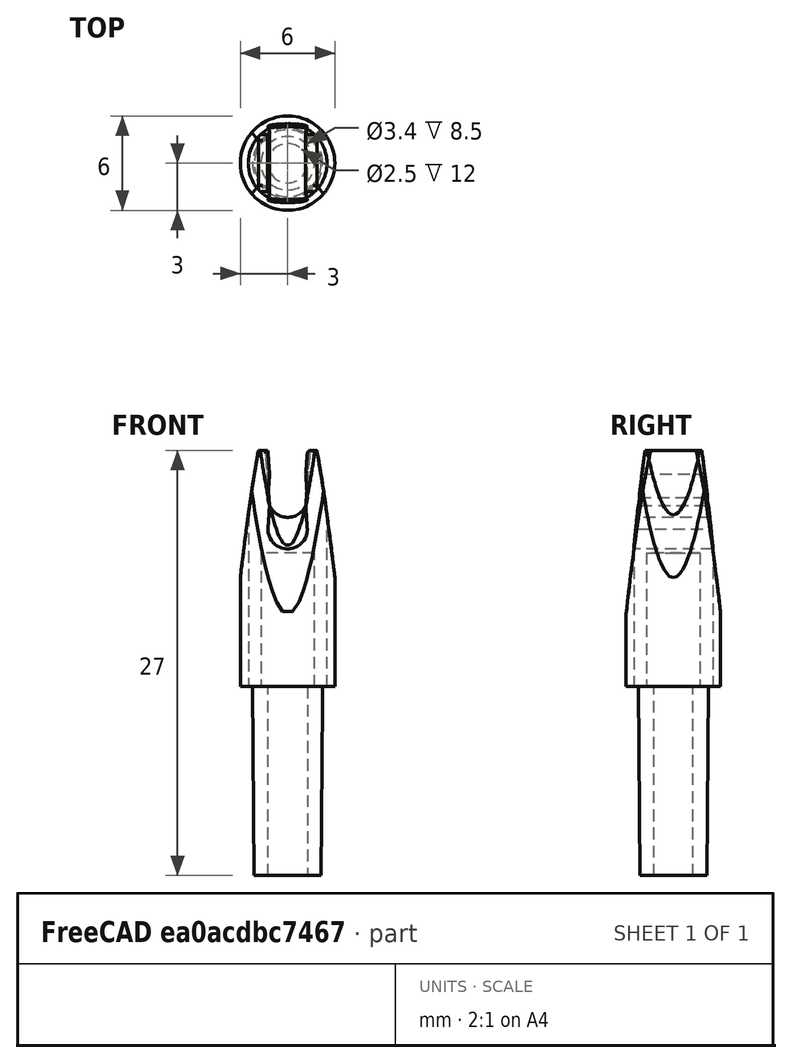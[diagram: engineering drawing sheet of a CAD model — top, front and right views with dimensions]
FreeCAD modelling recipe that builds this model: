
FCSTD DOCUMENT  (FreeCAD 0.20R26155 (Git))
Label: 4mm Pole Nock and 3mm Pin Nock
License: Creative Commons Attribution
LicenseURL: http://creativecommons.org/licenses/by/4.0/
objects: Sketcher::SketchObject×12, PartDesign::Pocket×8, PartDesign::Pad×3, PartDesign::Fillet×2, PartDesign::Body×2, Mesh::Feature×2
note: 40 computed .brp shape members not serialized (recipe doc carries the construction recipe); baked Part::Feature solids carry a one-line shape summary decoded from their .brp

FEATURE [Sketcher::SketchObject] Sketch
  FullyConstrained = true
  MapMode = 5
  Support = -> [XY_Plane]
  sketch-geometry (1):
    g0: Circle CenterX=0 CenterY=0 CenterZ=0 NormalX=0 NormalY=0 NormalZ=1 AngleXU=0 Radius=3
  constraints (2):
    c: Coincident(g0,g-1)
    c: Diameter(g0) = 6
FEATURE [PartDesign::Pad] Pad
  Direction = (0,0,1)
  Length = 15
  Length2 = 100
  Profile = -> Sketch
  Type = 0
FEATURE [Sketcher::SketchObject] Sketch001
  FullyConstrained = true
  MapMode = 5
  Placement = pos=(0,0,0) rot=(1,0,0;1.5708rad)
  Support = -> [XZ_Plane]
  sketch-geometry (6):
    g0: ArcOfCircle CenterX=0 CenterY=10 CenterZ=0 NormalX=0 NormalY=0 NormalZ=1 AngleXU=0 Radius=1.25 StartAngle=3.14159 EndAngle=6.28319
    g1: LineSegment StartX=-1.15 StartY=11.5 StartZ=0 EndX=-1.75 EndY=19.5 EndZ=0
    g2: LineSegment StartX=-1.75 StartY=19.5 StartZ=0 EndX=1.75 EndY=19.5 EndZ=0
    g3: LineSegment StartX=1.75 StartY=19.5 StartZ=0 EndX=1.15 EndY=11.5 EndZ=0
    g4: LineSegment StartX=1.15 StartY=11.5 StartZ=0 EndX=1.25 EndY=10 EndZ=0
    g5: LineSegment StartX=-1.15 StartY=11.5 StartZ=0 EndX=-1.25 EndY=10 EndZ=0
  constraints (17):
    c: PointOnObject(g0,g-2)
    c: Horizontal(g0,g0)
    c: Horizontal(g0,g0)
    c: DistanceX(g0,g0) = 2.5
    c: Coincident(g1,g2)
    c: Coincident(g2,g3)
    c: Coincident(g3,g4)
    c: Coincident(g4,g0)
    c: Coincident(g5,g1)
    c: Coincident(g5,g0)
    c: Symmetric(g1,g3,g-2)
    c: Symmetric(g2,g1,g-2)
    c: DistanceY(g-1,g0) = 10
    c: DistanceY(g0,g3) = 1.5
    c: DistanceY(g3,g2) = 8
    c: DistanceX(g2,g2) = 3.5
    c: DistanceX(g1,g3) = 2.3
FEATURE [PartDesign::Pocket] Pocket
  BaseFeature = -> Pad
  Length = 7
  Length2 = 100
  Midplane = true
  Profile = -> Sketch001
  Type = 0
FEATURE [Sketcher::SketchObject] Sketch002
  FullyConstrained = true
  MapMode = 5
  Support = -> [XY_Plane]
  sketch-geometry (1):
    g0: Circle CenterX=0 CenterY=0 CenterZ=0 NormalX=0 NormalY=0 NormalZ=1 AngleXU=0 Radius=2.225
  constraints (2):
    c: Coincident(g0,g-1)
    c: Diameter(g0) = 4.45
FEATURE [PartDesign::Pad] Pad001
  BaseFeature = -> Pocket
  Direction = (0,0,1)
  Length = 12
  Length2 = 100
  Profile = -> Sketch002
  ReferenceAxis = -> Sketch002 [N_Axis]
  Reversed = true
  Type = 0
FEATURE [Sketcher::SketchObject] Sketch003
  FullyConstrained = true
  MapMode = 5
  Support = -> [XY_Plane]
  sketch-geometry (1):
    g0: Circle CenterX=0 CenterY=0 CenterZ=0 NormalX=0 NormalY=0 NormalZ=1 AngleXU=0 Radius=1.25
  constraints (2):
    c: Coincident(g0,g-1)
    c: Diameter(g0) = 2.5
FEATURE [PartDesign::Pocket] Pocket001
  BaseFeature = -> Pad001
  Length = 18
  Length2 = 100
  Profile = -> Sketch003
  Type = 0
FEATURE [PartDesign::Fillet] Fillet  label="fillet"
  Base = -> Pocket001 [Face9,Edge17,Face3]
  BaseFeature = -> Pocket001
  Radius = 0.2
  SupportTransform = false
FEATURE [Sketcher::SketchObject] Sketch004
  FullyConstrained = false
  MapMode = 5
  Placement = pos=(0,0,0) rot=(1,0,0;1.5708rad)
  Support = -> [XZ_Plane]
  sketch-geometry (11):
    g0: LineSegment StartX=-6 StartY=4 StartZ=0 EndX=-6 EndY=22 EndZ=0
    g1: LineSegment StartX=-6 StartY=22 StartZ=0 EndX=6 EndY=22 EndZ=0
    g2: LineSegment StartX=6 StartY=22 StartZ=0 EndX=6 EndY=4 EndZ=0
    g3: LineSegment StartX=-6 StartY=4 StartZ=0 EndX=-3.31793 EndY=4 EndZ=0
    g4: LineSegment StartX=6 StartY=4 StartZ=0 EndX=3.31793 EndY=4 EndZ=0
    g5: Circle CenterX=-3.31793 CenterY=4 CenterZ=0 NormalX=0 NormalY=0 NormalZ=1 AngleXU=0 Radius=1
    g6: Circle CenterX=0 CenterY=36 CenterZ=0 NormalX=0 NormalY=0 NormalZ=1 AngleXU=0 Radius=1
    g7: Circle CenterX=3.31793 CenterY=4 CenterZ=0 NormalX=0 NormalY=0 NormalZ=1 AngleXU=0 Radius=1
    g8: BSplineCurve PolesCount=3 KnotsCount=2 Degree=2 IsPeriodic=0
    g9: GeomPoint X=-3.31793 Y=4 Z=0
    g10: GeomPoint X=3.31793 Y=4 Z=0
  constraints (24):
    c: Vertical(g0)
    c: Coincident(g0,g1)
    c: Coincident(g1,g2)
    c: Symmetric(g2,g0,g-2)
    c: Symmetric(g0,g1,g-2)
    c: Coincident(g3,g0)
    c: Horizontal(g3)
    c: Coincident(g4,g2)
    c: Symmetric(g3,g4,g-2)
    c: Coincident(g8,g3)
    c: Weight(g5) = 1
    c: Equal(g5,g6)
    c: PointOnObject(g6,g-2)
    c: Equal(g5,g7)
    c: Coincident(g8,g4)
    c: InternalAlignment(g5,g8)
    c: InternalAlignment(g6,g8)
    c: InternalAlignment(g7,g8)
    c: InternalAlignment(g9,g8)
    c: InternalAlignment(g10,g8)
    c: DistanceY(g-1,g0) = 4
    c: DistanceX(g1,g1) = 12
    c: DistanceY(g-1,g6) = 36
    c: DistanceY(g0,g0) = 18
FEATURE [PartDesign::Pocket] Pocket002
  BaseFeature = -> Fillet
  Length = 10
  Length2 = 100
  Midplane = true
  Profile = -> Sketch004
  Type = 0
FEATURE [Sketcher::SketchObject] Sketch005
  FullyConstrained = false
  MapMode = 5
  Placement = pos=(0,0,0) rot=(0.57735,0.57735,0.57735;2.0944rad)
  Support = -> [YZ_Plane]
  sketch-geometry (11):
    g0: LineSegment StartX=-3.13174 StartY=3.4287 StartZ=0 EndX=-10.6002 EndY=3.4287 EndZ=0
    g1: LineSegment StartX=-10.6002 StartY=3.4287 StartZ=0 EndX=-10.6002 EndY=40.5505 EndZ=0
    g2: LineSegment StartX=-10.6002 StartY=40.5505 StartZ=0 EndX=10.6002 EndY=40.5505 EndZ=0
    g3: LineSegment StartX=10.6002 StartY=40.5505 StartZ=0 EndX=10.6002 EndY=3.4287 EndZ=0
    g4: LineSegment StartX=10.6002 StartY=3.4287 StartZ=0 EndX=3.13174 EndY=3.4287 EndZ=0
    g5: Circle CenterX=-3.13174 CenterY=3.4287 CenterZ=0 NormalX=0 NormalY=0 NormalZ=1 AngleXU=0 Radius=1
    g6: Circle CenterX=0 CenterY=32.7419 CenterZ=0 NormalX=0 NormalY=0 NormalZ=1 AngleXU=0 Radius=1
    g7: Circle CenterX=3.13174 CenterY=3.4287 CenterZ=0 NormalX=0 NormalY=0 NormalZ=1 AngleXU=0 Radius=1
    g8: BSplineCurve PolesCount=3 KnotsCount=2 Degree=2 IsPeriodic=0
    g9: GeomPoint X=-3.13174 Y=3.4287 Z=0
    g10: GeomPoint X=3.13174 Y=3.4287 Z=0
  constraints (21):
    c: Horizontal(g0)
    c: Coincident(g0,g1)
    c: Vertical(g1)
    c: Coincident(g1,g2)
    c: Coincident(g2,g3)
    c: Vertical(g3)
    c: Coincident(g3,g4)
    c: Horizontal(g4)
    c: Symmetric(g0,g4,g-2)
    c: Symmetric(g1,g2,g-2)
    c: Coincident(g8,g0)
    c: Weight(g5) = 1
    c: Equal(g5,g6)
    c: PointOnObject(g6,g-2)
    c: Equal(g5,g7)
    c: Coincident(g8,g4)
    c: InternalAlignment(g5,g8)
    c: InternalAlignment(g6,g8)
    c: InternalAlignment(g7,g8)
    c: InternalAlignment(g9,g8)
    c: InternalAlignment(g10,g8)
FEATURE [PartDesign::Pocket] Pocket003  label="4mm Poll Nock"
  BaseFeature = -> Pocket002
  Length = 9
  Length2 = 100
  Midplane = true
  Profile = -> Sketch005
  Type = 0
FEATURE [PartDesign::Body] Body
  Group = -> [Sketch,Pad,Sketch001,Pocket,Sketch002,Pad001,Sketch003,Pocket001,Fillet,Sketch004,Pocket002,Sketch005,Pocket003]
  Origin = -> Origin
  Tip = -> Pocket003
FEATURE [Sketcher::SketchObject] Sketch006
  FullyConstrained = true
  MapMode = 5
  Support = -> [XY_Plane001]
  sketch-geometry (1):
    g0: Circle CenterX=0 CenterY=0 CenterZ=0 NormalX=0 NormalY=0 NormalZ=1 AngleXU=0 Radius=1.7
  constraints (2):
    c: Coincident(g0,g-1)
    c: Diameter(g0) = 3.4
FEATURE [Sketcher::SketchObject] Sketch007
  FullyConstrained = true
  MapMode = 5
  Placement = pos=(0,0,0) rot=(1,0,0;1.5708rad)
  Support = -> [XZ_Plane001]
  sketch-geometry (6):
    g0: ArcOfCircle CenterX=0 CenterY=12 CenterZ=0 NormalX=0 NormalY=0 NormalZ=1 AngleXU=0 Radius=1.25 StartAngle=3.14159 EndAngle=6.28319
    g1: LineSegment StartX=-1.15 StartY=13.5 StartZ=0 EndX=-1.75 EndY=21.5 EndZ=0
    g2: LineSegment StartX=-1.75 StartY=21.5 StartZ=0 EndX=1.75 EndY=21.5 EndZ=0
    g3: LineSegment StartX=1.75 StartY=21.5 StartZ=0 EndX=1.15 EndY=13.5 EndZ=0
    g4: LineSegment StartX=1.15 StartY=13.5 StartZ=0 EndX=1.25 EndY=12 EndZ=0
    g5: LineSegment StartX=-1.15 StartY=13.5 StartZ=0 EndX=-1.25 EndY=12 EndZ=0
  constraints (17):
    c: PointOnObject(g0,g-2)
    c: Horizontal(g0,g0)
    c: Horizontal(g0,g0)
    c: DistanceX(g0,g0) = 2.5
    c: Coincident(g1,g2)
    c: Coincident(g2,g3)
    c: Coincident(g3,g4)
    c: Coincident(g4,g0)
    c: Coincident(g5,g1)
    c: Coincident(g5,g0)
    c: Symmetric(g1,g3,g-2)
    c: Symmetric(g2,g1,g-2)
    c: DistanceY(g-1,g0) = 12
    c: DistanceY(g0,g3) = 1.5
    c: DistanceY(g3,g2) = 8
    c: DistanceX(g2,g2) = 3.5
    c: DistanceX(g1,g3) = 2.3
FEATURE [Sketcher::SketchObject] Sketch008
  FullyConstrained = false
  MapMode = 5
  Placement = pos=(0,0,0) rot=(1,0,0;1.5708rad)
  Support = -> [XZ_Plane001]
  sketch-geometry (11):
    g0: LineSegment StartX=-6 StartY=4 StartZ=0 EndX=-6 EndY=22 EndZ=0
    g1: LineSegment StartX=-6 StartY=22 StartZ=0 EndX=6 EndY=22 EndZ=0
    g2: LineSegment StartX=6 StartY=22 StartZ=0 EndX=6 EndY=4 EndZ=0
    g3: LineSegment StartX=-6 StartY=4 StartZ=0 EndX=-3.31793 EndY=4 EndZ=0
    g4: LineSegment StartX=6 StartY=4 StartZ=0 EndX=3.31793 EndY=4 EndZ=0
    g5: Circle CenterX=-3.31793 CenterY=4 CenterZ=0 NormalX=0 NormalY=0 NormalZ=1 AngleXU=0 Radius=1
    g6: Circle CenterX=0 CenterY=36 CenterZ=0 NormalX=0 NormalY=0 NormalZ=1 AngleXU=0 Radius=1
    g7: Circle CenterX=3.31793 CenterY=4 CenterZ=0 NormalX=0 NormalY=0 NormalZ=1 AngleXU=0 Radius=1
    g8: BSplineCurve PolesCount=3 KnotsCount=2 Degree=2 IsPeriodic=0
    g9: GeomPoint X=-3.31793 Y=4 Z=0
    g10: GeomPoint X=3.31793 Y=4 Z=0
  constraints (24):
    c: Vertical(g0)
    c: Coincident(g0,g1)
    c: Coincident(g1,g2)
    c: Symmetric(g2,g0,g-2)
    c: Symmetric(g0,g1,g-2)
    c: Coincident(g3,g0)
    c: Horizontal(g3)
    c: Coincident(g4,g2)
    c: Symmetric(g3,g4,g-2)
    c: Coincident(g8,g3)
    c: Weight(g5) = 1
    c: Equal(g5,g6)
    c: PointOnObject(g6,g-2)
    c: Equal(g5,g7)
    c: Coincident(g8,g4)
    c: InternalAlignment(g5,g8)
    c: InternalAlignment(g6,g8)
    c: InternalAlignment(g7,g8)
    c: InternalAlignment(g9,g8)
    c: InternalAlignment(g10,g8)
    c: DistanceY(g-1,g0) = 4
    c: DistanceX(g1,g1) = 12
    c: DistanceY(g-1,g6) = 36
    c: DistanceY(g0,g0) = 18
FEATURE [Sketcher::SketchObject] Sketch009
  FullyConstrained = false
  MapMode = 5
  Placement = pos=(0,0,0) rot=(0.57735,0.57735,0.57735;2.0944rad)
  Support = -> [YZ_Plane001]
  sketch-geometry (11):
    g0: LineSegment StartX=-2.99587 StartY=3.47483 StartZ=0 EndX=-10.6002 EndY=3.47483 EndZ=0
    g1: LineSegment StartX=-10.6002 StartY=3.47483 StartZ=0 EndX=-10.6002 EndY=40.5505 EndZ=0
    g2: LineSegment StartX=-10.6002 StartY=40.5505 StartZ=0 EndX=10.6002 EndY=40.5505 EndZ=0
    g3: LineSegment StartX=10.6002 StartY=40.5505 StartZ=0 EndX=10.6002 EndY=3.47483 EndZ=0
    g4: LineSegment StartX=10.6002 StartY=3.47483 StartZ=0 EndX=2.99587 EndY=3.47483 EndZ=0
    g5: Circle CenterX=-2.99587 CenterY=3.47483 CenterZ=0 NormalX=0 NormalY=0 NormalZ=1 AngleXU=0 Radius=1
    g6: Circle CenterX=0 CenterY=39.5827 CenterZ=0 NormalX=0 NormalY=0 NormalZ=1 AngleXU=0 Radius=1
    g7: Circle CenterX=2.99587 CenterY=3.47483 CenterZ=0 NormalX=0 NormalY=0 NormalZ=1 AngleXU=0 Radius=1
    g8: BSplineCurve PolesCount=3 KnotsCount=2 Degree=2 IsPeriodic=0
    g9: GeomPoint X=-2.99587 Y=3.47483 Z=0
    g10: GeomPoint X=2.99587 Y=3.47483 Z=0
  constraints (21):
    c: Horizontal(g0)
    c: Coincident(g0,g1)
    c: Vertical(g1)
    c: Coincident(g1,g2)
    c: Coincident(g2,g3)
    c: Vertical(g3)
    c: Coincident(g3,g4)
    c: Horizontal(g4)
    c: Symmetric(g0,g4,g-2)
    c: Symmetric(g1,g2,g-2)
    c: Coincident(g8,g0)
    c: Weight(g5) = 1
    c: Equal(g5,g6)
    c: PointOnObject(g6,g-2)
    c: Equal(g5,g7)
    c: Coincident(g8,g4)
    c: InternalAlignment(g5,g8)
    c: InternalAlignment(g6,g8)
    c: InternalAlignment(g7,g8)
    c: InternalAlignment(g9,g8)
    c: InternalAlignment(g10,g8)
FEATURE [Sketcher::SketchObject] Sketch010
  FullyConstrained = true
  MapMode = 5
  Support = -> [XY_Plane001]
  sketch-geometry (1):
    g0: Circle CenterX=0 CenterY=0 CenterZ=0 NormalX=0 NormalY=0 NormalZ=1 AngleXU=0 Radius=2.5
  constraints (2):
    c: Coincident(g0,g-1)
    c: Diameter(g0) = 5
FEATURE [Sketcher::SketchObject] Sketch011
  FullyConstrained = true
  MapMode = 5
  Support = -> [XY_Plane001]
  sketch-geometry (1):
    g0: Circle CenterX=0 CenterY=0 CenterZ=0 NormalX=0 NormalY=0 NormalZ=1 AngleXU=0 Radius=2.175
  constraints (2):
    c: Coincident(g0,g-1)
    c: Diameter(g0) = 4.35
FEATURE [PartDesign::Pad] Pad003
  Direction = (1,1,1)
  Length = 15
  Length2 = 100
  Profile = -> Sketch010
  Type = 0
FEATURE [PartDesign::Pocket] Pocket006
  BaseFeature = -> Pad003
  Length = 7
  Length2 = 100
  Midplane = true
  Profile = -> Sketch007
  Type = 0
FEATURE [PartDesign::Pocket] Pocket007
  BaseFeature = -> Pocket006
  Length = 8.5
  Length2 = 100
  Profile = -> Sketch006
  Reversed = true
  Type = 0
FEATURE [PartDesign::Fillet] Fillet001  label="fillet001"
  Base = -> Pocket007 [Face3,Edge17,Face3]
  BaseFeature = -> Pocket007
  Radius = 0.2
  SupportTransform = false
FEATURE [PartDesign::Pocket] Pocket005
  BaseFeature = -> Fillet001
  Length = 10
  Length2 = 100
  Midplane = true
  Profile = -> Sketch008
  Type = 0
FEATURE [PartDesign::Pocket] Pocket004  label="3mm Pin Nock001"
  BaseFeature = -> Pocket005
  Length = 9
  Length2 = 100
  Midplane = true
  Profile = -> Sketch009
  Type = 0
FEATURE [PartDesign::Body] Body001
  Group = -> [Sketch010,Pad003,Sketch007,Pocket006,Sketch011,Sketch006,Pocket007,Fillet001,Sketch008,Pocket005,Sketch009,Pocket004]
  Origin = -> Origin001
  Tip = -> Pocket004
FEATURE [Mesh::Feature] Mesh  label="3mm Pin Nock001 (Meshed)"
FEATURE [Mesh::Feature] Mesh001  label="4mm Poll Nock (Meshed)"
